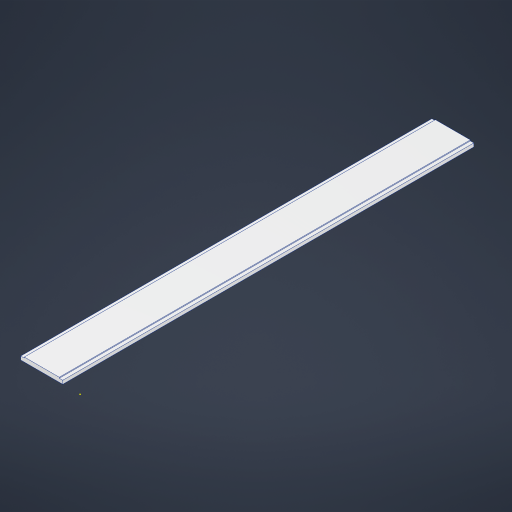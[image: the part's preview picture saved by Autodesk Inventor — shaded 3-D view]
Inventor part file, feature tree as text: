
AUTODESK INVENTOR PART (.ipt)
format: ipt  version: 2024 (Build 280153000, 153)  size: 193,536 bytes
history: native  units: mm
features: sketch x3, extrude x2
ambient origin geometry x8: Origin, YZ Plane, XZ Plane, XY Plane, X Axis, Y Axis, Z Axis, Center Point
bodies: Solid1 (feature_tree)
feature tree (5):
  extrude  "Extrusion1"  Depth=96.0mm
  sketch  "Sketch2"  dims[d2=14.0mm d3=0.0mm d4=8.0mm]
  extrude  "Extrusion2"  Depth=8.0mm
  sketch  "Sketch1"  dims[d0=940.0mm d1=96.0mm]
  sketch  "Sketch3"  dims[d5=6.0mm d6=6.0mm d7=0.0mm d8=0.0mm]
